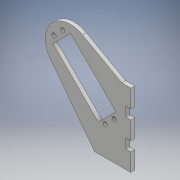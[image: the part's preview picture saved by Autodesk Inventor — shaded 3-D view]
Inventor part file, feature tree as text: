
AUTODESK INVENTOR PART (.ipt)
format: ipt  version: 2018 (Build 220112000, 112)  size: 128,000 bytes
history: native  units: mm
features: other x1, extrude x1, sketch x1
ambient origin geometry x8: Origin, YZ Plane, XZ Plane, XY Plane, X Axis, Y Axis, Z Axis, Center Point
bodies: Body1 (feature_tree)
feature tree (3):
  other  "Sólido1"
  extrude  "Extrusión1"  Depth=14.0mm
  sketch  "Boceto1"  dims[d17=3.0mm d21=14.0mm d22=14.0mm d25=14.0mm d26=30.0mm d107=3.0mm d108=0.0mm d109=7.5mm d110=7.5mm d111=4.0mm d112=57.0mm]
